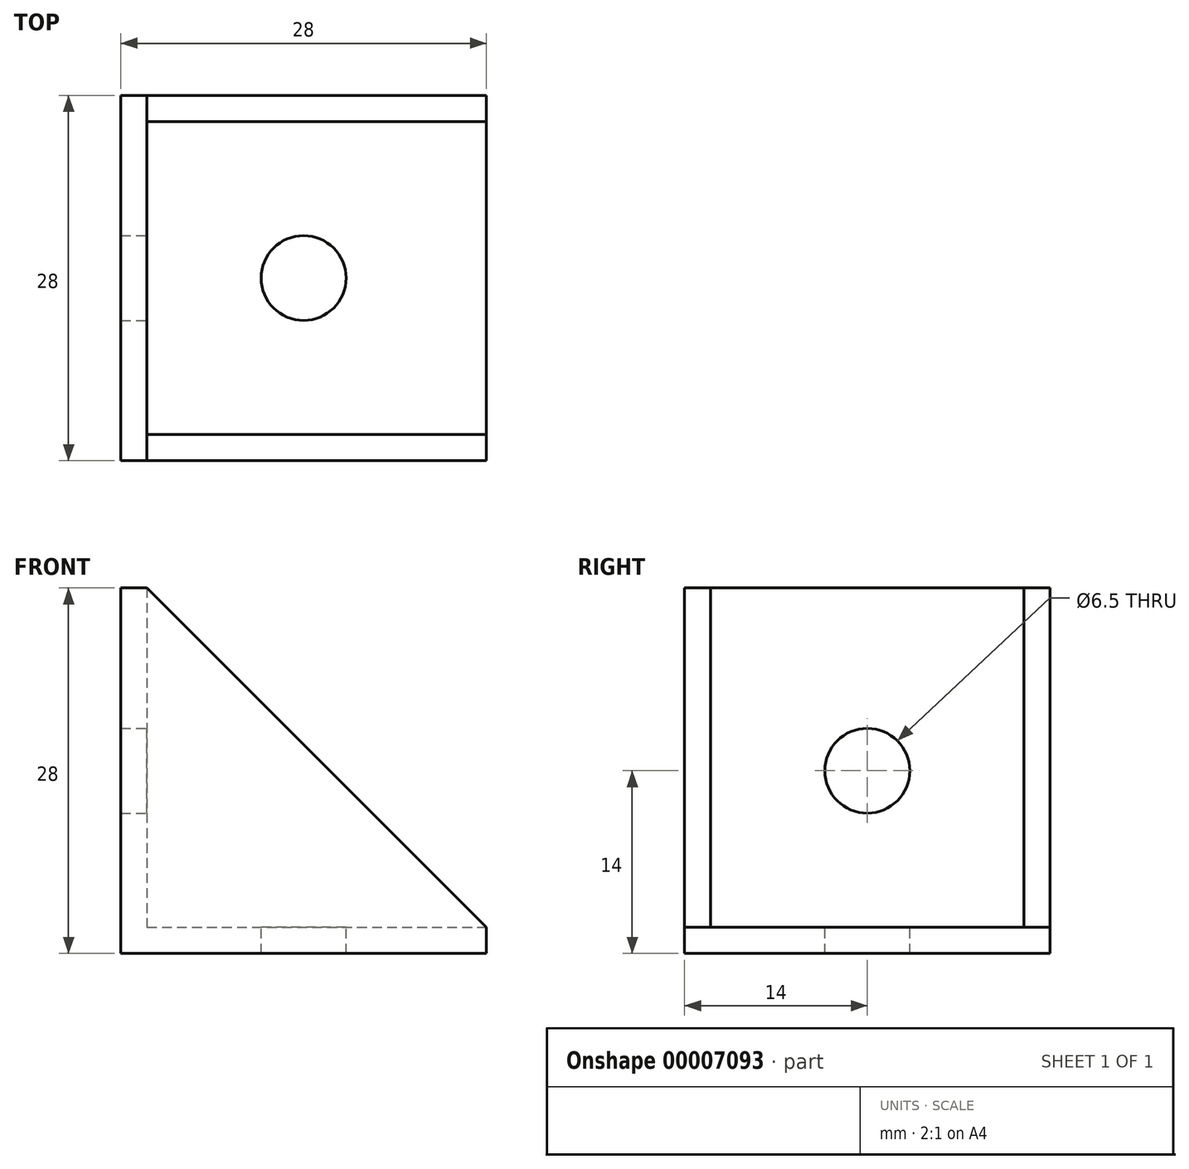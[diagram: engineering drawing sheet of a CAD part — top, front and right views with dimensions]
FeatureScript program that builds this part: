
annotation { "Feature Type Name" : "Feature", "Feature Type Description" : "" }
export const myFeature = defineFeature(function(context is Context, id is Id, definition is map)
    precondition{}
    {
        {
            var Q0;
            Q0=qCreatedBy(makeId("Front.planeOp"),FACE);
            var sketch = newSketch(context, id + "F0", { "sketchPlane" : qUnion([Q0])});
            skLineSegment(sketch, "E0.rect.bottom", {"start": v(14, -14) * mm, "end": v(-14, -14) * mm});
            skLineSegment(sketch, "E0.rect.top", {"start": v(14, 14) * mm, "end": v(-14, 14) * mm});
            skLineSegment(sketch, "E0.rect.left", {"start": v(14, -14) * mm, "end": v(14, 14) * mm});
            skLineSegment(sketch, "E0.rect.right", {"start": v(-14, -14) * mm, "end": v(-14, 14) * mm});
            skPoint(sketch, "E0.rect.middle", {"position": v(0, 0) * mm});
            skSolve(sketch);
        }
        {
            var Q0;
            Q0=makeQuery(id+"F0.imprint","IMPRINT",FACE,{"disambiguationData":[TD([[makeQuery(id+"F0.imprint","IMPRINT",EDGE,{"derivedFrom":sQuery(id+"F0.wireOp",EDGE,"E0.rect.bottom")}),-1.0]])]});
            extrude(context, id + "F1", {"entities" : qUnion([Q0]), "endBound" : BoundingType.SYMMETRIC, "depth" : 28 * mm});
        }
        {
            var Q0;
            Q0=makeQuery(id+"F1.opExtrude","CAP_FACE",FACE,{"disambiguationData":[OSD([sQuery(id+"F0.wireOp",EDGE,"E0.rect.bottom"),sQuery(id+"F0.wireOp",EDGE,"E0.rect.top"),sQuery(id+"F0.wireOp",EDGE,"E0.rect.left"),sQuery(id+"F0.wireOp",EDGE,"E0.rect.right")])],"isStart":false});
            var sketch = newSketch(context, id + "F2", { "sketchPlane" : qUnion([Q0])});
            skLineSegment(sketch, "E1", {"start": v(-12, 14) * mm, "end": v(14, -12) * mm});
            skLineSegment(sketch, "E2", {"start": v(14, -12) * mm, "end": v(14, -14) * mm});
            skLineSegment(sketch, "E3", {"start": v(-14, 14) * mm, "end": v(-12, 14) * mm});
            skSolve(sketch);
        }
        {
            var Q0;
            {var subQ1=sQuery(id+"F2.wireOp",EDGE,"E1");Q0=makeQuery(id+"F2.imprint","IMPRINT",FACE,{"disambiguationData":[TD([[makeQuery(id+"F2.imprint","IMPRINT",EDGE,{"derivedFrom":subQ1}),1.0]])]});}
            extrude(context, id + "F3", {"entities" : qUnion([Q0]), "operationType" : NewBodyOperationType.REMOVE, "endBound" : BoundingType.THROUGH_ALL, "oppositeDirection" : true, "depth" : 25 * mm});
        }
        {
            var Q0;
            Q0=qCreatedBy(makeId("Front.planeOp"),FACE);
            var sketch = newSketch(context, id + "F4", { "sketchPlane" : qUnion([Q0])});
            skLineSegment(sketch, "E4.bottom", {"start": v(-12, 14) * mm, "end": v(14, 14) * mm});
            skLineSegment(sketch, "E4.top", {"start": v(-12, -12) * mm, "end": v(14, -12) * mm});
            skLineSegment(sketch, "E4.left", {"start": v(-12, 14) * mm, "end": v(-12, -12) * mm});
            skLineSegment(sketch, "E4.right", {"start": v(14, 14) * mm, "end": v(14, -12) * mm});
            skSolve(sketch);
        }
        {
            var Q0;
            Q0=makeQuery(id+"F4.imprint","IMPRINT",FACE,{"disambiguationData":[TD([[makeQuery(id+"F4.imprint","IMPRINT",EDGE,{"derivedFrom":sQuery(id+"F4.wireOp",EDGE,"E4.bottom")}),-1.0]])]});
            extrude(context, id + "F5", {"entities" : qUnion([Q0]), "operationType" : NewBodyOperationType.REMOVE, "endBound" : BoundingType.SYMMETRIC, "oppositeDirection" : true, "depth" : (28 - 4) * mm});
        }
        {
            var Q0;
            Q0=makeQuery(id+"F5.boolean.opBoolean","COPY",FACE,{"derivedFrom":makeQuery(id+"F5.opExtrude","SWEPT_FACE",FACE,{"disambiguationData":[OSD([sQuery(id+"F4.wireOp",EDGE,"E4.top")])]})});
            var sketch = newSketch(context, id + "F6", { "sketchPlane" : qUnion([Q0])});
            skCircle(sketch, "E5", {"center": v(0, 0) * mm, "radius": 3.25 * mm});
            skSolve(sketch);
        }
        {
            var Q0;
            Q0=makeQuery(id+"F6.imprint","IMPRINT",FACE,{"disambiguationData":[TD([[makeQuery(id+"F6.imprint","IMPRINT",EDGE,{"derivedFrom":sQuery(id+"F6.wireOp",EDGE,"E5")}),1.0]])]});
            extrude(context, id + "F7", {"entities" : qUnion([Q0]), "operationType" : NewBodyOperationType.REMOVE, "endBound" : BoundingType.THROUGH_ALL, "oppositeDirection" : true, "depth" : 25 * mm});
        }
        {
            var Q0;
            Q0=makeQuery(id+"F5.boolean.opBoolean","COPY",FACE,{"derivedFrom":makeQuery(id+"F5.opExtrude","SWEPT_FACE",FACE,{"disambiguationData":[OSD([sQuery(id+"F4.wireOp",EDGE,"E4.left")])]})});
            var sketch = newSketch(context, id + "F8", { "sketchPlane" : qUnion([Q0])});
            skCircle(sketch, "E6", {"center": v(0, 0) * mm, "radius": 3.25 * mm});
            skSolve(sketch);
        }
        {
            var Q0;
            Q0=makeQuery(id+"F8.imprint","IMPRINT",FACE,{"disambiguationData":[TD([[makeQuery(id+"F8.imprint","IMPRINT",EDGE,{"derivedFrom":sQuery(id+"F8.wireOp",EDGE,"E6")}),1.0]])]});
            extrude(context, id + "F9", {"entities" : qUnion([Q0]), "operationType" : NewBodyOperationType.REMOVE, "endBound" : BoundingType.THROUGH_ALL, "oppositeDirection" : true, "depth" : 25 * mm});
        }
    });
